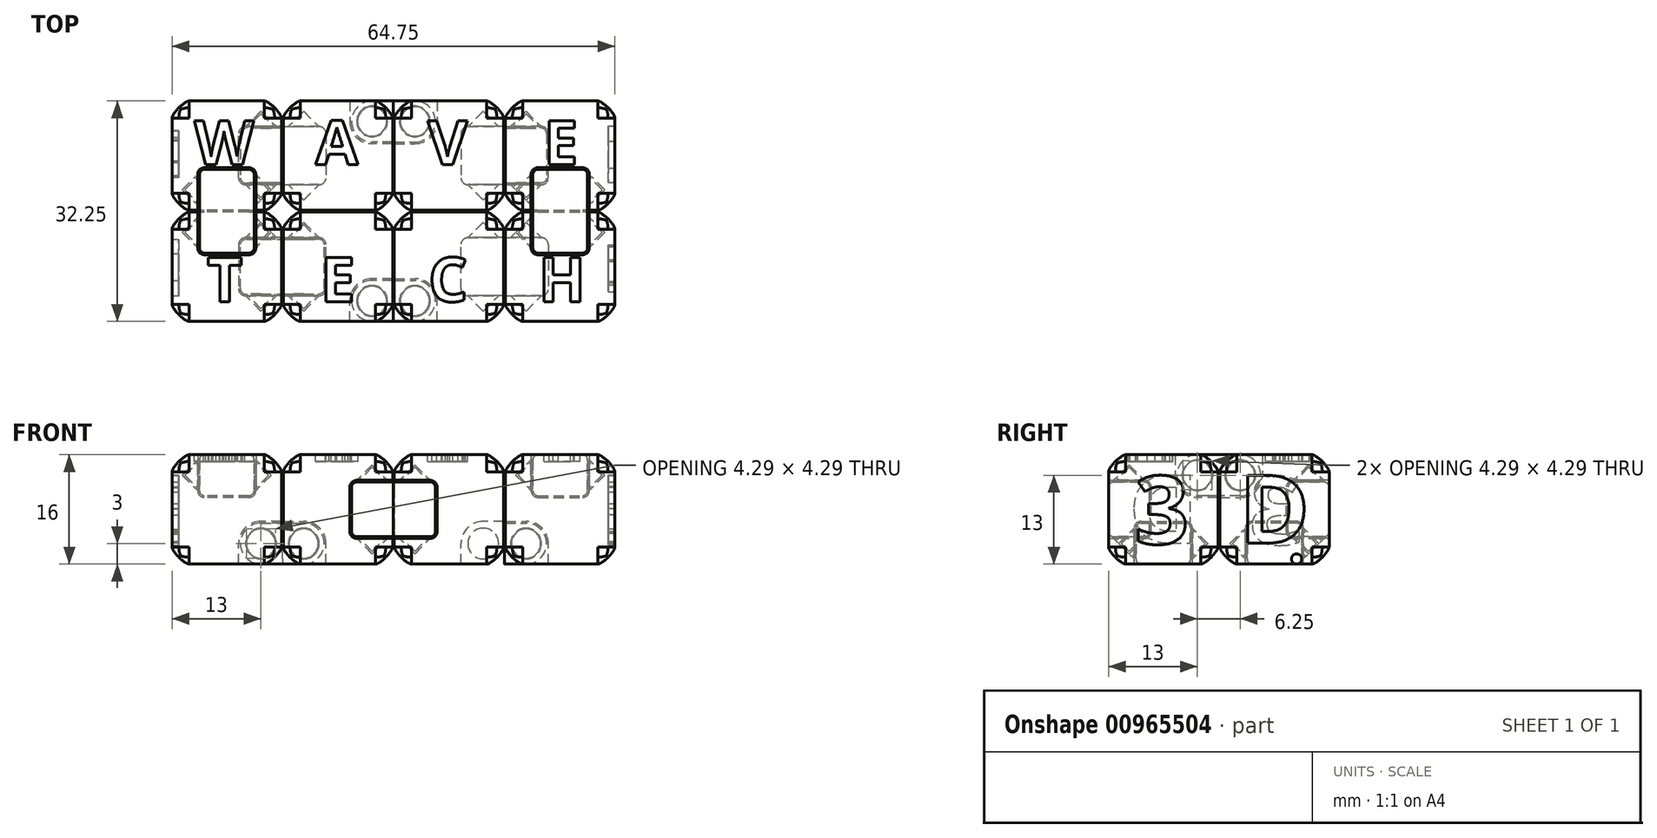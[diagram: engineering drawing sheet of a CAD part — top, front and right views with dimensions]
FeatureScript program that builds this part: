
annotation { "Feature Type Name" : "Feature", "Feature Type Description" : "" }
export const myFeature = defineFeature(function(context is Context, id is Id, definition is map)
    precondition{}
    {
        {
            assignVariable(context, id + "F0", {"name" : "cubeSize", "anyValue" : 16});
        }
        {
            assignVariable(context, id + "F1", {"name" : "hingeSize", "anyValue" : getVariable(context, 'cubeSize') / 2});
        }
        {
            assignVariable(context, id + "F2", {"name" : "hingeDiameter", "anyValue" : getVariable(context, 'hingeSize') / 2});
        }
        {
            assignVariable(context, id + "F3", {"name" : "minThickness", "anyValue" : 1});
        }
        {
            assignVariable(context, id + "F4", {"name" : "hingeGap", "anyValue" : .25});
        }
        {
            var Q0;
            Q0=qCreatedBy(makeId("Top.planeOp"),FACE);
            var sketch = newSketch(context, id + "F5", { "sketchPlane" : qUnion([Q0])});
            skLineSegment(sketch, "E0.bottom", {"start": v(8, -8) * mm, "end": v(-8, -8) * mm});
            skLineSegment(sketch, "E0.top", {"start": v(8, 8) * mm, "end": v(-8, 8) * mm});
            skLineSegment(sketch, "E0.left", {"start": v(8, -8) * mm, "end": v(8, 8) * mm});
            skLineSegment(sketch, "E0.right", {"start": v(-8, -8) * mm, "end": v(-8, 8) * mm});
            skPoint(sketch, "E0.middle", {"position": v(0, 0) * mm});
            skSolve(sketch);
        }
        {
            var Q0;
            Q0=qSketchRegion(id+"F5",true);
            extrude(context, id + "F6", {"entities" : qUnion([Q0]), "depth" : (getVariable(context, 'cubeSize')) * mm, "offsetDistance" : 25 * mm});
        }
        {
            var Q0;
            Q0=qCreatedBy(makeId("Front.planeOp"),FACE);
            var sketch = newSketch(context, id + "F7", { "sketchPlane" : qUnion([Q0])});
            skCircle(sketch, "E1", {"center": v(5, 3) * mm, "radius": 2 * mm});
            skLineSegment(sketch, "E2", {"start": v(5, 3) * mm, "end": v(7, 3) * mm, "construction": true});
            skLineSegment(sketch, "E3", {"start": v(7, 3) * mm, "end": v(8, 3) * mm, "construction": true});
            skLineSegment(sketch, "E4", {"start": v(5, 0) * mm, "end": v(5, 1) * mm, "construction": true});
            skLineSegment(sketch, "E5", {"start": v(5, 1) * mm, "end": v(5, 3) * mm, "construction": true});
            skLineSegment(sketch, "E6", {"start": v(8, 0) * mm, "end": v(1.75, 0) * mm});
            skLineSegment(sketch, "E7", {"start": v(1.75, 0) * mm, "end": v(1.75, 3) * mm});
            skLineSegment(sketch, "E8", {"start": v(8, 0) * mm, "end": v(8, 6.25) * mm});
            skLineSegment(sketch, "E9", {"start": v(8, 6.25) * mm, "end": v(5, 6.25) * mm});
            skArc(sketch, "E10", {"start": v(5, 6.25) * mm, "mid": v(2.7, 5.3) * mm, "end": v(1.75, 3) * mm});
            skSolve(sketch);
        }
        {
            var Q0;
            Q0=makeQuery(id+"F7.imprint","IMPRINT",FACE,{"disambiguationData":[TD([[makeQuery(id+"F7.imprint","IMPRINT",EDGE,{"derivedFrom":sQuery(id+"F7.wireOp",EDGE,"E1")}),-1.0]])]});
            var Q1;
            Q1=makeQuery(id+"F7.imprint","IMPRINT",FACE,{"disambiguationData":[TD([[makeQuery(id+"F7.imprint","IMPRINT",EDGE,{"derivedFrom":sQuery(id+"F7.wireOp",EDGE,"E1")}),1.0]])]});
            extrude(context, id + "F8", {"entities" : qUnion([Q0, Q1]), "operationType" : NewBodyOperationType.REMOVE, "endBound" : BoundingType.SYMMETRIC, "oppositeDirection" : true, "depth" : (getVariable(context, 'hingeSize') + getVariable(context, 'hingeGap') * 2) * mm, "offsetDistance" : 25 * mm});
        }
        {
            var Q0;
            Q0=makeQuery(id+"F6.opExtrude","CAP_VERTEX",VERTEX,{"disambiguationData":[OSD([sQuery(id+"F5.wireOp",EDGE,"E0.bottom"),sQuery(id+"F5.wireOp",EDGE,"E0.right")])],"isStart":false});
            var Q1;
            Q1=makeQuery(id+"F6.opExtrude","CAP_VERTEX",VERTEX,{"disambiguationData":[OSD([sQuery(id+"F5.wireOp",EDGE,"E0.bottom"),sQuery(id+"F5.wireOp",EDGE,"E0.left")])],"isStart":true});
            var Q2;
            Q2=makeQuery(id+"F6.opExtrude","CAP_VERTEX",VERTEX,{"disambiguationData":[OSD([sQuery(id+"F5.wireOp",EDGE,"E0.top"),sQuery(id+"F5.wireOp",EDGE,"E0.left")])],"isStart":true});
            cPlane(context, id + "F9", {"entities" : qUnion([Q0, Q1, Q2]), "cplaneType" : CPlaneType.THREE_POINT, "offset" : 25 * mm, "width" : 150 * mm, "height" : 150 * mm});
        }
        {
            var Q0;
            Q0=qCreatedBy(id+"F9.planeOp",FACE);
            var sketch = newSketch(context, id + "F10", { "sketchPlane" : qUnion([Q0])});
            skLineSegment(sketch, "E11", {"start": v(4.25, 0.84) * mm, "end": v(-4.25, 0.84) * mm});
            skLineSegment(sketch, "E12", {"start": v(-4.25, 0.84) * mm, "end": v(-6.5, -1.41) * mm});
            skLineSegment(sketch, "E13", {"start": v(-6.5, -1.41) * mm, "end": v(6.5, -1.41) * mm});
            skLineSegment(sketch, "E14", {"start": v(6.5, -1.41) * mm, "end": v(4.25, 0.84) * mm});
            skSolve(sketch);
        }
        {
            var Q0;
            Q0=makeQuery(id+"F10.imprint","IMPRINT",FACE,{"disambiguationData":[TD([[makeQuery(id+"F10.imprint","IMPRINT",EDGE,{"derivedFrom":sQuery(id+"F10.wireOp",EDGE,"E11")}),1.0]])]});
            var Q1;
            Q1=sQuery(id+"F10.wireOp",EDGE,"E13");
            revolve(context, id + "F11", {"operationType" : NewBodyOperationType.REMOVE, "entities" : qUnion([Q0]), "axis" : qUnion([Q1]), "revolveType" : RevolveType.FULL, "oppositeDirection" : true});
        }
        {
            var Q0;
            Q0=qCreatedBy(makeId("Right.planeOp"),FACE);
            var sketch = newSketch(context, id + "F12", { "sketchPlane" : qUnion([Q0])});
            skCircle(sketch, "E15", {"center": v(5, 13) * mm, "radius": 2 * mm});
            skLineSegment(sketch, "E16", {"start": v(1.75, 16) * mm, "end": v(8, 16) * mm});
            skLineSegment(sketch, "E17", {"start": v(8, 16) * mm, "end": v(8, 9.75) * mm});
            skLineSegment(sketch, "E18", {"start": v(8, 9.75) * mm, "end": v(5, 9.75) * mm});
            skLineSegment(sketch, "E19", {"start": v(1.75, 16) * mm, "end": v(1.75, 13) * mm});
            skLineSegment(sketch, "E20", {"start": v(5, 13) * mm, "end": v(7, 13) * mm, "construction": true});
            skLineSegment(sketch, "E21", {"start": v(7, 13) * mm, "end": v(8, 13) * mm, "construction": true});
            skLineSegment(sketch, "E22", {"start": v(5, 13) * mm, "end": v(5, 15) * mm, "construction": true});
            skLineSegment(sketch, "E23", {"start": v(5, 15) * mm, "end": v(5, 16) * mm, "construction": true});
            skArc(sketch, "E24", {"start": v(1.75, 13) * mm, "mid": v(2.7, 10.7) * mm, "end": v(5, 9.75) * mm});
            skSolve(sketch);
        }
        {
            var Q0;
            Q0=makeQuery(id+"F12.imprint","IMPRINT",FACE,{"disambiguationData":[TD([[makeQuery(id+"F12.imprint","IMPRINT",EDGE,{"derivedFrom":sQuery(id+"F12.wireOp",EDGE,"E15")}),1.0]])]});
            var Q1;
            Q1=makeQuery(id+"F12.imprint","IMPRINT",FACE,{"disambiguationData":[TD([[makeQuery(id+"F12.imprint","IMPRINT",EDGE,{"derivedFrom":sQuery(id+"F12.wireOp",EDGE,"E15")}),-1.0]])]});
            extrude(context, id + "F13", {"entities" : qUnion([Q0, Q1]), "operationType" : NewBodyOperationType.REMOVE, "endBound" : BoundingType.SYMMETRIC, "depth" : (getVariable(context, 'hingeSize') + getVariable(context, 'hingeGap') * 2) * mm, "offsetDistance" : 25 * mm});
        }
        {
            var Q0;
            Q0=makeQuery(id+"F6.opExtrude","CAP_VERTEX",VERTEX,{"disambiguationData":[OSD([sQuery(id+"F5.wireOp",EDGE,"E0.top"),sQuery(id+"F5.wireOp",EDGE,"E0.left")])],"isStart":false});
            var Q1;
            Q1=makeQuery(id+"F6.opExtrude","CAP_VERTEX",VERTEX,{"disambiguationData":[OSD([sQuery(id+"F5.wireOp",EDGE,"E0.top"),sQuery(id+"F5.wireOp",EDGE,"E0.right")])],"isStart":false});
            var Q2;
            Q2=makeQuery(id+"F6.opExtrude","CAP_VERTEX",VERTEX,{"disambiguationData":[OSD([sQuery(id+"F5.wireOp",EDGE,"E0.bottom"),sQuery(id+"F5.wireOp",EDGE,"E0.right")])],"isStart":true});
            cPlane(context, id + "F14", {"entities" : qUnion([Q0, Q1, Q2]), "cplaneType" : CPlaneType.THREE_POINT, "offset" : 25 * mm, "width" : 150 * mm, "height" : 150 * mm});
        }
        {
            var Q0;
            Q0=qCreatedBy(id+"F14.planeOp",FACE);
            var sketch = newSketch(context, id + "F15", { "sketchPlane" : qUnion([Q0])});
            skLineSegment(sketch, "E25", {"start": v(-6.5, 12.73) * mm, "end": v(6.5, 12.73) * mm});
            skLineSegment(sketch, "E26", {"start": v(6.5, 12.73) * mm, "end": v(4.25, 10.48) * mm});
            skLineSegment(sketch, "E27", {"start": v(4.25, 10.48) * mm, "end": v(-4.25, 10.48) * mm});
            skLineSegment(sketch, "E28", {"start": v(-4.25, 10.48) * mm, "end": v(-6.5, 12.73) * mm});
            skSolve(sketch);
        }
        {
            var Q0;
            Q0=qSketchRegion(id+"F15",true);
            var Q1;
            Q1=sQuery(id+"F15.wireOp",EDGE,"E25");
            revolve(context, id + "F16", {"operationType" : NewBodyOperationType.REMOVE, "entities" : qUnion([Q0]), "axis" : qUnion([Q1]), "revolveType" : RevolveType.FULL, "oppositeDirection" : true});
        }
        {
            var Q0;
            Q0=makeQuery(id+"F6.opExtrude","SWEPT_FACE",FACE,{"disambiguationData":[OSD([sQuery(id+"F5.wireOp",EDGE,"E0.right")])]});
            var Q1;
            Q1=makeQuery(id+"F6.opExtrude","SWEPT_FACE",FACE,{"disambiguationData":[OSD([sQuery(id+"F5.wireOp",EDGE,"E0.bottom")])]});
            var Q2;
            {var subQ0=sQuery(id+"F5.wireOp",EDGE,"E0.right");var subQ1=sQuery(id+"F5.wireOp",EDGE,"E0.top");Q2=makeQuery(id+"F13.boolean.opBoolean","SPLIT",EDGE,{"disambiguationData":[TD([makeQuery(id+"F6.opExtrude","SWEPT_FACE",FACE,{"disambiguationData":[OSD([subQ0])]})])],"derivedFrom":makeQuery(id+"F6.opExtrude","CAP_EDGE",EDGE,{"disambiguationData":[OSD([subQ1])],"isStart":false})});}
            var Q3;
            {var subQ0=sQuery(id+"F5.wireOp",EDGE,"E0.left");var subQ1=sQuery(id+"F5.wireOp",EDGE,"E0.top");Q3=makeQuery(id+"F13.boolean.opBoolean","SPLIT",EDGE,{"disambiguationData":[TD([makeQuery(id+"F6.opExtrude","SWEPT_FACE",FACE,{"disambiguationData":[OSD([subQ0])]})])],"derivedFrom":makeQuery(id+"F6.opExtrude","CAP_EDGE",EDGE,{"disambiguationData":[OSD([subQ1])],"isStart":false})});}
            var Q4;
            Q4=makeQuery(id+"F6.opExtrude","CAP_EDGE",EDGE,{"disambiguationData":[OSD([sQuery(id+"F5.wireOp",EDGE,"E0.left")])],"isStart":false});
            var Q5;
            Q5=makeQuery(id+"F6.opExtrude","SWEPT_EDGE",EDGE,{"disambiguationData":[OSD([sQuery(id+"F5.wireOp",EDGE,"E0.top"),sQuery(id+"F5.wireOp",EDGE,"E0.left")])]});
            var Q6;
            {var subQ0=sQuery(id+"F5.wireOp",EDGE,"E0.left");var subQ1=sQuery(id+"F5.wireOp",EDGE,"E0.top");Q6=makeQuery(id+"F8.boolean.opBoolean","SPLIT",EDGE,{"disambiguationData":[TD([makeQuery(id+"F6.opExtrude","SWEPT_FACE",FACE,{"disambiguationData":[OSD([subQ1])]})])],"derivedFrom":makeQuery(id+"F6.opExtrude","CAP_EDGE",EDGE,{"disambiguationData":[OSD([subQ0])],"isStart":true})});}
            var Q7;
            Q7=makeQuery(id+"F6.opExtrude","CAP_EDGE",EDGE,{"disambiguationData":[OSD([sQuery(id+"F5.wireOp",EDGE,"E0.top")])],"isStart":true});
            var Q8;
            {var subQ0=sQuery(id+"F5.wireOp",EDGE,"E0.bottom");var subQ1=sQuery(id+"F5.wireOp",EDGE,"E0.left");Q8=makeQuery(id+"F8.boolean.opBoolean","SPLIT",EDGE,{"disambiguationData":[TD([makeQuery(id+"F6.opExtrude","SWEPT_FACE",FACE,{"disambiguationData":[OSD([subQ0])]})])],"derivedFrom":makeQuery(id+"F6.opExtrude","CAP_EDGE",EDGE,{"disambiguationData":[OSD([subQ1])],"isStart":true})});}
            fillet(context, id + "F17", {"entities" : qUnion([Q0, Q1, Q2, Q3, Q4, Q5, Q6, Q7, Q8]), "radius" : (getVariable(context, 'hingeDiameter') / 2 + getVariable(context, 'minThickness') - .5) * mm, "tangentPropagation" : true, "rho" : .2, "crossSection" : FilletCrossSection.CONIC, "allowEdgeOverflow" : false});
        }
        {
            var Q0;
            Q0=makeQuery(id+"F8.boolean.opBoolean","COPY",EDGE,{"derivedFrom":makeQuery(id+"F8.opExtrude","CAP_EDGE",EDGE,{"disambiguationData":[OSD([sQuery(id+"F7.wireOp",EDGE,"E7")])],"isStart":true})});
            var Q1;
            Q1=makeQuery(id+"F8.boolean.opBoolean","COPY",EDGE,{"derivedFrom":makeQuery(id+"F8.opExtrude","CAP_EDGE",EDGE,{"disambiguationData":[OSD([sQuery(id+"F7.wireOp",EDGE,"E7")])],"isStart":false})});
            var Q2;
            Q2=makeQuery(id+"F13.boolean.opBoolean","COPY",EDGE,{"derivedFrom":makeQuery(id+"F13.opExtrude","CAP_EDGE",EDGE,{"disambiguationData":[OSD([sQuery(id+"F12.wireOp",EDGE,"E18")])],"isStart":false})});
            var Q3;
            Q3=makeQuery(id+"F13.boolean.opBoolean","COPY",EDGE,{"derivedFrom":makeQuery(id+"F13.opExtrude","CAP_EDGE",EDGE,{"disambiguationData":[OSD([sQuery(id+"F12.wireOp",EDGE,"E18")])],"isStart":true})});
            fillet(context, id + "F18", {"entities" : qUnion([Q0, Q1, Q2, Q3]), "radius" : (getVariable(context, 'minThickness')) * mm, "tangentPropagation" : true, "allowEdgeOverflow" : false});
        }
        {
            var Q0;
            Q0=qCreatedBy(makeId("Front.planeOp"),FACE);
            var sketch = newSketch(context, id + "F19", { "sketchPlane" : qUnion([Q0])});
            skCircle(sketch, "E29", {"center": v(5, 3) * mm, "radius": 2 * mm, "construction": true});
            skArc(sketch, "E30", {"start": v(5, 6) * mm, "mid": v(2, 3) * mm, "end": v(5, 0) * mm});
            skArc(sketch, "E31", {"start": v(11.25, 0) * mm, "mid": v(14.25, 3) * mm, "end": v(11.25, 6) * mm});
            skLineSegment(sketch, "E32", {"start": v(5, 3) * mm, "end": v(8, 3) * mm, "construction": true});
            skCircle(sketch, "E33", {"center": v(11.25, 3) * mm, "radius": 2 * mm, "construction": true});
            skLineSegment(sketch, "E34", {"start": v(8, 3) * mm, "end": v(8.25, 3) * mm, "construction": true});
            skLineSegment(sketch, "E35", {"start": v(8.25, 3) * mm, "end": v(11.25, 3) * mm, "construction": true});
            skLineSegment(sketch, "E36", {"start": v(8.12, 0) * mm, "end": v(8.12, 3) * mm});
            skLineSegment(sketch, "E37", {"start": v(8.12, 3) * mm, "end": v(8.12, 6) * mm});
            skLineSegment(sketch, "E38", {"start": v(11.25, 0) * mm, "end": v(5, 0) * mm});
            skLineSegment(sketch, "E39", {"start": v(11.25, 6) * mm, "end": v(5, 6) * mm});
            skSolve(sketch);
        }
        {
            var Q0;
            Q0=makeQuery(id+"F19.imprint","IMPRINT",FACE,{"disambiguationData":[TD([[makeQuery(id+"F19.imprint","IMPRINT",EDGE,{"derivedFrom":sQuery(id+"F19.wireOp",EDGE,"E30")}),1.0]])]});
            extrude(context, id + "F20", {"entities" : qUnion([Q0]), "endBound" : BoundingType.SYMMETRIC, "depth" : (getVariable(context, 'hingeSize')) * mm, "offsetDistance" : 25 * mm});
        }
        {
            var Q0;
            Q0=qCreatedBy(id+"F9.planeOp",FACE);
            var sketch = newSketch(context, id + "F21", { "sketchPlane" : qUnion([Q0])});
            skLineSegment(sketch, "E40", {"start": v(6.15, -1.41) * mm, "end": v(3.9, 0.84) * mm});
            skLineSegment(sketch, "E41", {"start": v(3.9, 0.84) * mm, "end": v(-3.9, 0.84) * mm});
            skLineSegment(sketch, "E42", {"start": v(-3.9, 0.84) * mm, "end": v(-6.15, -1.41) * mm});
            skLineSegment(sketch, "E43", {"start": v(-6.15, -1.41) * mm, "end": v(6.15, -1.41) * mm});
            skSolve(sketch);
        }
        {
            var Q0;
            Q0=qSketchRegion(id+"F21",true);
            var Q1;
            Q1=sQuery(id+"F21.wireOp",EDGE,"E43");
            revolve(context, id + "F22", {"operationType" : NewBodyOperationType.ADD, "entities" : qUnion([Q0]), "axis" : qUnion([Q1]), "revolveType" : RevolveType.FULL});
        }
        {
            var Q0;
            Q0=qCreatedBy(makeId("Right.planeOp"),FACE);
            var sketch = newSketch(context, id + "F23", { "sketchPlane" : qUnion([Q0])});
            skCircle(sketch, "E44", {"center": v(5, 13) * mm, "radius": 2.25 * mm, "construction": true});
            skArc(sketch, "E45", {"start": v(5, 16) * mm, "mid": v(2, 13) * mm, "end": v(5, 10) * mm});
            skArc(sketch, "E46", {"start": v(11.25, 10) * mm, "mid": v(14.25, 13) * mm, "end": v(11.25, 16) * mm});
            skLineSegment(sketch, "E47", {"start": v(5, 13) * mm, "end": v(8, 13) * mm, "construction": true});
            skCircle(sketch, "E48", {"center": v(11.25, 13) * mm, "radius": 2 * mm, "construction": true});
            skLineSegment(sketch, "E49", {"start": v(8, 13) * mm, "end": v(8.25, 13) * mm, "construction": true});
            skLineSegment(sketch, "E50", {"start": v(8.25, 13) * mm, "end": v(11.25, 13) * mm, "construction": true});
            skLineSegment(sketch, "E51", {"start": v(8.12, 10) * mm, "end": v(8.12, 13) * mm});
            skLineSegment(sketch, "E52", {"start": v(8.12, 13) * mm, "end": v(8.12, 16) * mm});
            skLineSegment(sketch, "E53", {"start": v(11.25, 10) * mm, "end": v(5, 10) * mm});
            skLineSegment(sketch, "E54", {"start": v(11.25, 16) * mm, "end": v(5, 16) * mm});
            skSolve(sketch);
        }
        {
            var Q0;
            {var subQ3=sQuery(id+"F23.wireOp",EDGE,"E45");Q0=makeQuery(id+"F23.imprint","IMPRINT",FACE,{"disambiguationData":[TD([[makeQuery(id+"F23.imprint","IMPRINT",EDGE,{"derivedFrom":subQ3}),1.0]])]});}
            extrude(context, id + "F24", {"entities" : qUnion([Q0]), "endBound" : BoundingType.SYMMETRIC, "depth" : (getVariable(context, 'hingeSize')) * mm, "offsetDistance" : 25 * mm});
        }
        {
            var Q0;
            Q0=makeQuery(id+"F20.opExtrude","CAP_EDGE",EDGE,{"disambiguationData":[OSD([sQuery(id+"F19.wireOp",EDGE,"E38")])],"isStart":false});
            var Q1;
            Q1=makeQuery(id+"F20.opExtrude","CAP_EDGE",EDGE,{"disambiguationData":[OSD([sQuery(id+"F19.wireOp",EDGE,"E38")])],"isStart":true});
            var Q2;
            Q2=makeQuery(id+"F24.opExtrude","CAP_EDGE",EDGE,{"disambiguationData":[OSD([sQuery(id+"F23.wireOp",EDGE,"E54")])],"isStart":false});
            var Q3;
            Q3=makeQuery(id+"F24.opExtrude","CAP_EDGE",EDGE,{"disambiguationData":[OSD([sQuery(id+"F23.wireOp",EDGE,"E54")])],"isStart":true});
            fillet(context, id + "F25", {"entities" : qUnion([Q0, Q1, Q2, Q3]), "radius" : (getVariable(context, 'minThickness') - getVariable(context, 'hingeGap')) * mm, "tangentPropagation" : true, "allowEdgeOverflow" : false});
        }
        {
            var Q0;
            Q0=qCreatedBy(id+"F14.planeOp",FACE);
            var sketch = newSketch(context, id + "F26", { "sketchPlane" : qUnion([Q0])});
            skLineSegment(sketch, "E55", {"start": v(-6.15, 12.73) * mm, "end": v(6.15, 12.73) * mm});
            skLineSegment(sketch, "E56", {"start": v(6.15, 12.73) * mm, "end": v(3.9, 10.48) * mm});
            skLineSegment(sketch, "E57", {"start": v(3.9, 10.48) * mm, "end": v(-3.9, 10.48) * mm});
            skLineSegment(sketch, "E58", {"start": v(-3.9, 10.48) * mm, "end": v(-6.15, 12.73) * mm});
            skSolve(sketch);
        }
        {
            var Q0;
            Q0=makeQuery(id+"F26.imprint","IMPRINT",FACE,{"disambiguationData":[TD([[makeQuery(id+"F26.imprint","IMPRINT",EDGE,{"derivedFrom":sQuery(id+"F26.wireOp",EDGE,"E55")}),-1.0]])]});
            var Q1;
            Q1=sQuery(id+"F26.wireOp",EDGE,"E55");
            revolve(context, id + "F27", {"operationType" : NewBodyOperationType.ADD, "entities" : qUnion([Q0]), "axis" : qUnion([Q1]), "revolveType" : RevolveType.FULL});
        }
        {
            var Q0;
            Q0=makeQuery(id+"F20.opExtrude","SWEPT_FACE",FACE,{"disambiguationData":[OSD([sQuery(id+"F19.wireOp",EDGE,"E36"),sQuery(id+"F19.wireOp",EDGE,"E37")])]});
            var sketch = newSketch(context, id + "F28", { "sketchPlane" : qUnion([Q0])});
            skLineSegment(sketch, "E59", {"start": v(-7.63, -0.12) * mm, "end": v(6.67, -0.12) * mm, "construction": true});
            skSolve(sketch);
        }
        {
            var Q0;
            Q0=makeQuery(id+"F6.opExtrude","SWEPT_BODY",BODY,{"disambiguationData":[OSD([sQuery(id+"F5.wireOp",EDGE,"E0.bottom"),sQuery(id+"F5.wireOp",EDGE,"E0.top"),sQuery(id+"F5.wireOp",EDGE,"E0.left"),sQuery(id+"F5.wireOp",EDGE,"E0.right")])]});
            var Q1;
            Q1=makeQuery(id+"F24.opExtrude","SWEPT_BODY",BODY,{"disambiguationData":[OSD([sQuery(id+"F23.wireOp",EDGE,"E45"),sQuery(id+"F23.wireOp",EDGE,"E51"),sQuery(id+"F23.wireOp",EDGE,"E52"),sQuery(id+"F23.wireOp",EDGE,"E53"),sQuery(id+"F23.wireOp",EDGE,"E54")])]});
            var Q2;
            Q2=sQuery(id+"F28.wireOp",EDGE,"E59");
            circularPattern(context, id + "F29", {"entities" : qUnion([Q0, Q1]), "axis" : qUnion([Q2]), "angle" : 90 * degree, "instanceCount" : 2});
        }
        {
            var Q0;
            Q0=makeQuery(id+"F29.opPattern","COPY",BODY,{"derivedFrom":makeQuery(id+"F6.opExtrude","SWEPT_BODY",BODY,{"disambiguationData":[OSD([sQuery(id+"F5.wireOp",EDGE,"E0.bottom"),sQuery(id+"F5.wireOp",EDGE,"E0.top"),sQuery(id+"F5.wireOp",EDGE,"E0.left"),sQuery(id+"F5.wireOp",EDGE,"E0.right")])]}),"instanceName":"1"});
            var Q1;
            Q1=makeQuery(id+"F29.opPattern","COPY",BODY,{"derivedFrom":makeQuery(id+"F24.opExtrude","SWEPT_BODY",BODY,{"disambiguationData":[OSD([sQuery(id+"F23.wireOp",EDGE,"E45"),sQuery(id+"F23.wireOp",EDGE,"E51"),sQuery(id+"F23.wireOp",EDGE,"E52"),sQuery(id+"F23.wireOp",EDGE,"E53"),sQuery(id+"F23.wireOp",EDGE,"E54")])]}),"instanceName":"1"});
            var Q2;
            Q2=qCreatedBy(makeId("Front.planeOp"),FACE);
            mirror(context, id + "F30", {"entities" : qUnion([Q0, Q1]), "mirrorPlane" : qUnion([Q2])});
        }
        {
            var Q0;
            Q0=makeQuery(id+"F29.opPattern","COPY",BODY,{"derivedFrom":makeQuery(id+"F24.opExtrude","SWEPT_BODY",BODY,{"disambiguationData":[OSD([sQuery(id+"F23.wireOp",EDGE,"E45"),sQuery(id+"F23.wireOp",EDGE,"E51"),sQuery(id+"F23.wireOp",EDGE,"E52"),sQuery(id+"F23.wireOp",EDGE,"E53"),sQuery(id+"F23.wireOp",EDGE,"E54")])]}),"instanceName":"1"});
            var Q1;
            Q1=makeQuery(id+"F29.opPattern","COPY",BODY,{"derivedFrom":makeQuery(id+"F6.opExtrude","SWEPT_BODY",BODY,{"disambiguationData":[OSD([sQuery(id+"F5.wireOp",EDGE,"E0.bottom"),sQuery(id+"F5.wireOp",EDGE,"E0.top"),sQuery(id+"F5.wireOp",EDGE,"E0.left"),sQuery(id+"F5.wireOp",EDGE,"E0.right")])]}),"instanceName":"1"});
            deleteBodies(context, id + "F31", {"entities" : qUnion([Q0, Q1])});
        }
        {
            var Q0;
            Q0=makeQuery(id+"F20.opExtrude","SWEPT_BODY",BODY,{"disambiguationData":[OSD([sQuery(id+"F19.wireOp",EDGE,"E30"),sQuery(id+"F19.wireOp",EDGE,"E36"),sQuery(id+"F19.wireOp",EDGE,"E37"),sQuery(id+"F19.wireOp",EDGE,"E38"),sQuery(id+"F19.wireOp",EDGE,"E39")])]});
            var Q1;
            Q1=makeQuery(id+"F20.opExtrude","SWEPT_FACE",FACE,{"disambiguationData":[OSD([sQuery(id+"F19.wireOp",EDGE,"E36"),sQuery(id+"F19.wireOp",EDGE,"E37")])]});
            mirror(context, id + "F32", {"operationType" : NewBodyOperationType.ADD, "entities" : qUnion([Q0]), "mirrorPlane" : qUnion([Q1])});
        }
        {
            var Q0;
            {var subQ0=sQuery(id+"F5.wireOp",EDGE,"E0.left");var subQ1=makeQuery(id+"F6.opExtrude","SWEPT_FACE",FACE,{"disambiguationData":[OSD([subQ0])]});var subQ2=sQuery(id+"F5.wireOp",EDGE,"E0.bottom");Q0=makeQuery(id+"F30.opPattern","COPY",VERTEX,{"derivedFrom":makeQuery(id+"F29.opPattern","COPY",VERTEX,{"derivedFrom":makeQuery(id+"F17.opFillet","BLEND_VERTEX",VERTEX,{"blendedFrom":[makeQuery(id+"F6.opExtrude","CAP_VERTEX",VERTEX,{"disambiguationData":[OSD([subQ2,subQ0])],"isStart":true}),makeQuery(id+"F6.opExtrude","SWEPT_EDGE",EDGE,{"disambiguationData":[OSD([subQ2,subQ0])]}),makeQuery(id+"F8.boolean.opBoolean","SPLIT",EDGE,{"disambiguationData":[TD([makeQuery(id+"F6.opExtrude","SWEPT_FACE",FACE,{"disambiguationData":[OSD([subQ2])]})])],"derivedFrom":makeQuery(id+"F6.opExtrude","CAP_EDGE",EDGE,{"disambiguationData":[OSD([subQ0])],"isStart":true})}),subQ1],"blendedInto":[subQ1]}),"instanceName":"1"}),"instanceName":"1"});}
            var Q1;
            {var subQ0=sQuery(id+"F5.wireOp",EDGE,"E0.left");var subQ1=sQuery(id+"F5.wireOp",EDGE,"E0.top");Q1=makeQuery(id+"F30.opPattern","COPY",VERTEX,{"derivedFrom":makeQuery(id+"F29.opPattern","COPY",VERTEX,{"derivedFrom":makeQuery(id+"F17.opFillet","BLEND_VERTEX",VERTEX,{"blendedFrom":[makeQuery(id+"F6.opExtrude","CAP_VERTEX",VERTEX,{"disambiguationData":[OSD([subQ1,subQ0])],"isStart":false}),makeQuery(id+"F6.opExtrude","SWEPT_EDGE",EDGE,{"disambiguationData":[OSD([subQ1,subQ0])]}),makeQuery(id+"F6.opExtrude","CAP_EDGE",EDGE,{"disambiguationData":[OSD([subQ0])],"isStart":false}),makeQuery(id+"F6.opExtrude","SWEPT_FACE",FACE,{"disambiguationData":[OSD([subQ0])]})],"blendedInto":[makeQuery(id+"F6.opExtrude","SWEPT_FACE",FACE,{"disambiguationData":[OSD([subQ0])]})]}),"instanceName":"1"}),"instanceName":"1"});}
            var Q2;
            {var subQ0=sQuery(id+"F5.wireOp",EDGE,"E0.right");var subQ1=sQuery(id+"F5.wireOp",EDGE,"E0.top");Q2=makeQuery(id+"F30.opPattern","COPY",VERTEX,{"derivedFrom":makeQuery(id+"F29.opPattern","COPY",VERTEX,{"derivedFrom":makeQuery(id+"F17.opFillet","BLEND_VERTEX",VERTEX,{"blendedFrom":[makeQuery(id+"F6.opExtrude","CAP_VERTEX",VERTEX,{"disambiguationData":[OSD([subQ1,subQ0])],"isStart":false}),makeQuery(id+"F6.opExtrude","SWEPT_EDGE",EDGE,{"disambiguationData":[OSD([subQ1,subQ0])]}),makeQuery(id+"F6.opExtrude","CAP_EDGE",EDGE,{"disambiguationData":[OSD([subQ0])],"isStart":false}),makeQuery(id+"F6.opExtrude","SWEPT_FACE",FACE,{"disambiguationData":[OSD([subQ0])]})],"blendedInto":[makeQuery(id+"F6.opExtrude","SWEPT_FACE",FACE,{"disambiguationData":[OSD([subQ0])]})]}),"instanceName":"1"}),"instanceName":"1"});}
            cPlane(context, id + "F33", {"entities" : qUnion([Q0, Q1, Q2]), "cplaneType" : CPlaneType.THREE_POINT, "offset" : 25 * mm, "width" : 150 * mm, "height" : 150 * mm});
        }
        {
            var Q0;
            Q0=qCreatedBy(id+"F33.planeOp",FACE);
            var sketch = newSketch(context, id + "F34", { "sketchPlane" : qUnion([Q0])});
            skLineSegment(sketch, "E60", {"start": v(-18.56, 14.15) * mm, "end": v(-18.56, 1.85) * mm, "construction": true});
            skSolve(sketch);
        }
        {
            var Q0;
            Q0=makeQuery(id+"F30.opPattern","COPY",BODY,{"derivedFrom":makeQuery(id+"F29.opPattern","COPY",BODY,{"derivedFrom":makeQuery(id+"F24.opExtrude","SWEPT_BODY",BODY,{"disambiguationData":[OSD([sQuery(id+"F23.wireOp",EDGE,"E45"),sQuery(id+"F23.wireOp",EDGE,"E51"),sQuery(id+"F23.wireOp",EDGE,"E52"),sQuery(id+"F23.wireOp",EDGE,"E53"),sQuery(id+"F23.wireOp",EDGE,"E54")])]}),"instanceName":"1"}),"instanceName":"1"});
            var Q1;
            Q1=sQuery(id+"F34.wireOp",EDGE,"E60");
            circularPattern(context, id + "F35", {"entities" : qUnion([Q0]), "axis" : qUnion([Q1]), "angle" : 90 * degree, "instanceCount" : 2, "oppositeDirection" : true});
        }
        {
            var Q0;
            Q0=makeQuery(id+"F30.opPattern","COPY",BODY,{"derivedFrom":makeQuery(id+"F29.opPattern","COPY",BODY,{"derivedFrom":makeQuery(id+"F24.opExtrude","SWEPT_BODY",BODY,{"disambiguationData":[OSD([sQuery(id+"F23.wireOp",EDGE,"E45"),sQuery(id+"F23.wireOp",EDGE,"E51"),sQuery(id+"F23.wireOp",EDGE,"E52"),sQuery(id+"F23.wireOp",EDGE,"E53"),sQuery(id+"F23.wireOp",EDGE,"E54")])]}),"instanceName":"1"}),"instanceName":"1"});
            deleteBodies(context, id + "F36", {"entities" : qUnion([Q0])});
        }
        {
            var Q0;
            Q0=makeQuery(id+"F24.opExtrude","SWEPT_BODY",BODY,{"disambiguationData":[OSD([sQuery(id+"F23.wireOp",EDGE,"E45"),sQuery(id+"F23.wireOp",EDGE,"E51"),sQuery(id+"F23.wireOp",EDGE,"E52"),sQuery(id+"F23.wireOp",EDGE,"E53"),sQuery(id+"F23.wireOp",EDGE,"E54")])]});
            var Q1;
            Q1=makeQuery(id+"F6.opExtrude","SWEPT_BODY",BODY,{"disambiguationData":[OSD([sQuery(id+"F5.wireOp",EDGE,"E0.bottom"),sQuery(id+"F5.wireOp",EDGE,"E0.top"),sQuery(id+"F5.wireOp",EDGE,"E0.left"),sQuery(id+"F5.wireOp",EDGE,"E0.right")])]});
            var Q2;
            Q2=makeQuery(id+"F20.opExtrude","SWEPT_BODY",BODY,{"disambiguationData":[OSD([sQuery(id+"F19.wireOp",EDGE,"E30"),sQuery(id+"F19.wireOp",EDGE,"E36"),sQuery(id+"F19.wireOp",EDGE,"E37"),sQuery(id+"F19.wireOp",EDGE,"E38"),sQuery(id+"F19.wireOp",EDGE,"E39")])]});
            var Q3;
            Q3=makeQuery(id+"F30.opPattern","COPY",BODY,{"derivedFrom":makeQuery(id+"F29.opPattern","COPY",BODY,{"derivedFrom":makeQuery(id+"F6.opExtrude","SWEPT_BODY",BODY,{"disambiguationData":[OSD([sQuery(id+"F5.wireOp",EDGE,"E0.bottom"),sQuery(id+"F5.wireOp",EDGE,"E0.top"),sQuery(id+"F5.wireOp",EDGE,"E0.left"),sQuery(id+"F5.wireOp",EDGE,"E0.right")])]}),"instanceName":"1"}),"instanceName":"1"});
            var Q4;
            Q4=makeQuery(id+"F35.opPattern","COPY",BODY,{"derivedFrom":makeQuery(id+"F30.opPattern","COPY",BODY,{"derivedFrom":makeQuery(id+"F29.opPattern","COPY",BODY,{"derivedFrom":makeQuery(id+"F24.opExtrude","SWEPT_BODY",BODY,{"disambiguationData":[OSD([sQuery(id+"F23.wireOp",EDGE,"E45"),sQuery(id+"F23.wireOp",EDGE,"E51"),sQuery(id+"F23.wireOp",EDGE,"E52"),sQuery(id+"F23.wireOp",EDGE,"E53"),sQuery(id+"F23.wireOp",EDGE,"E54")])]}),"instanceName":"1"}),"instanceName":"1"}),"instanceName":"1"});
            var Q5;
            Q5=makeQuery(id+"F24.opExtrude","SWEPT_FACE",FACE,{"disambiguationData":[OSD([sQuery(id+"F23.wireOp",EDGE,"E51"),sQuery(id+"F23.wireOp",EDGE,"E52")])]});
            mirror(context, id + "F37", {"operationType" : NewBodyOperationType.ADD, "entities" : qUnion([Q0, Q1, Q2, Q3, Q4]), "mirrorPlane" : qUnion([Q5])});
        }
        {
            var Q0;
            Q0=makeQuery(id+"F35.opPattern","COPY",BODY,{"derivedFrom":makeQuery(id+"F30.opPattern","COPY",BODY,{"derivedFrom":makeQuery(id+"F29.opPattern","COPY",BODY,{"derivedFrom":makeQuery(id+"F24.opExtrude","SWEPT_BODY",BODY,{"disambiguationData":[OSD([sQuery(id+"F23.wireOp",EDGE,"E45"),sQuery(id+"F23.wireOp",EDGE,"E51"),sQuery(id+"F23.wireOp",EDGE,"E52"),sQuery(id+"F23.wireOp",EDGE,"E53"),sQuery(id+"F23.wireOp",EDGE,"E54")])]}),"instanceName":"1"}),"instanceName":"1"}),"instanceName":"1"});
            var Q1;
            Q1=makeQuery(id+"F37.opPattern","COPY",BODY,{"derivedFrom":makeQuery(id+"F35.opPattern","COPY",BODY,{"derivedFrom":makeQuery(id+"F30.opPattern","COPY",BODY,{"derivedFrom":makeQuery(id+"F29.opPattern","COPY",BODY,{"derivedFrom":makeQuery(id+"F24.opExtrude","SWEPT_BODY",BODY,{"disambiguationData":[OSD([sQuery(id+"F23.wireOp",EDGE,"E45"),sQuery(id+"F23.wireOp",EDGE,"E51"),sQuery(id+"F23.wireOp",EDGE,"E52"),sQuery(id+"F23.wireOp",EDGE,"E53"),sQuery(id+"F23.wireOp",EDGE,"E54")])]}),"instanceName":"1"}),"instanceName":"1"}),"instanceName":"1"}),"instanceName":"1"});
            var Q2;
            Q2=makeQuery(id+"F24.opExtrude","SWEPT_BODY",BODY,{"disambiguationData":[OSD([sQuery(id+"F23.wireOp",EDGE,"E45"),sQuery(id+"F23.wireOp",EDGE,"E51"),sQuery(id+"F23.wireOp",EDGE,"E52"),sQuery(id+"F23.wireOp",EDGE,"E53"),sQuery(id+"F23.wireOp",EDGE,"E54")])]});
            var Q3;
            Q3=makeQuery(id+"F37.opPattern","COPY",BODY,{"derivedFrom":makeQuery(id+"F20.opExtrude","SWEPT_BODY",BODY,{"disambiguationData":[OSD([sQuery(id+"F19.wireOp",EDGE,"E30"),sQuery(id+"F19.wireOp",EDGE,"E36"),sQuery(id+"F19.wireOp",EDGE,"E37"),sQuery(id+"F19.wireOp",EDGE,"E38"),sQuery(id+"F19.wireOp",EDGE,"E39")])]}),"instanceName":"1"});
            var Q4;
            Q4=makeQuery(id+"F20.opExtrude","SWEPT_BODY",BODY,{"disambiguationData":[OSD([sQuery(id+"F19.wireOp",EDGE,"E30"),sQuery(id+"F19.wireOp",EDGE,"E36"),sQuery(id+"F19.wireOp",EDGE,"E37"),sQuery(id+"F19.wireOp",EDGE,"E38"),sQuery(id+"F19.wireOp",EDGE,"E39")])]});
            var Q5;
            Q5=makeQuery(id+"F37.opPattern","COPY",BODY,{"derivedFrom":makeQuery(id+"F30.opPattern","COPY",BODY,{"derivedFrom":makeQuery(id+"F29.opPattern","COPY",BODY,{"derivedFrom":makeQuery(id+"F6.opExtrude","SWEPT_BODY",BODY,{"disambiguationData":[OSD([sQuery(id+"F5.wireOp",EDGE,"E0.bottom"),sQuery(id+"F5.wireOp",EDGE,"E0.top"),sQuery(id+"F5.wireOp",EDGE,"E0.left"),sQuery(id+"F5.wireOp",EDGE,"E0.right")])]}),"instanceName":"1"}),"instanceName":"1"}),"instanceName":"1"});
            var Q6;
            Q6=makeQuery(id+"F37.opPattern","COPY",BODY,{"derivedFrom":makeQuery(id+"F6.opExtrude","SWEPT_BODY",BODY,{"disambiguationData":[OSD([sQuery(id+"F5.wireOp",EDGE,"E0.bottom"),sQuery(id+"F5.wireOp",EDGE,"E0.top"),sQuery(id+"F5.wireOp",EDGE,"E0.left"),sQuery(id+"F5.wireOp",EDGE,"E0.right")])]}),"instanceName":"1"});
            var Q7;
            Q7=makeQuery(id+"F6.opExtrude","SWEPT_BODY",BODY,{"disambiguationData":[OSD([sQuery(id+"F5.wireOp",EDGE,"E0.bottom"),sQuery(id+"F5.wireOp",EDGE,"E0.top"),sQuery(id+"F5.wireOp",EDGE,"E0.left"),sQuery(id+"F5.wireOp",EDGE,"E0.right")])]});
            var Q8;
            Q8=makeQuery(id+"F30.opPattern","COPY",BODY,{"derivedFrom":makeQuery(id+"F29.opPattern","COPY",BODY,{"derivedFrom":makeQuery(id+"F6.opExtrude","SWEPT_BODY",BODY,{"disambiguationData":[OSD([sQuery(id+"F5.wireOp",EDGE,"E0.bottom"),sQuery(id+"F5.wireOp",EDGE,"E0.top"),sQuery(id+"F5.wireOp",EDGE,"E0.left"),sQuery(id+"F5.wireOp",EDGE,"E0.right")])]}),"instanceName":"1"}),"instanceName":"1"});
            var Q9;
            Q9=makeQuery(id+"F35.opPattern","COPY",FACE,{"derivedFrom":makeQuery(id+"F30.opPattern","COPY",FACE,{"derivedFrom":makeQuery(id+"F29.opPattern","COPY",FACE,{"derivedFrom":makeQuery(id+"F24.opExtrude","SWEPT_FACE",FACE,{"disambiguationData":[OSD([sQuery(id+"F23.wireOp",EDGE,"E51"),sQuery(id+"F23.wireOp",EDGE,"E52")])]}),"instanceName":"1"}),"instanceName":"1"}),"instanceName":"1"});
            mirror(context, id + "F38", {"operationType" : NewBodyOperationType.ADD, "entities" : qUnion([Q0, Q1, Q2, Q3, Q4, Q5, Q6, Q7, Q8]), "mirrorPlane" : qUnion([Q9])});
        }
        {
            var Q0;
            Q0=makeQuery(id+"F37.opPattern","COPY",FACE,{"derivedFrom":makeQuery(id+"F30.opPattern","COPY",FACE,{"derivedFrom":makeQuery(id+"F29.opPattern","COPY",FACE,{"derivedFrom":makeQuery(id+"F6.opExtrude","SWEPT_FACE",FACE,{"disambiguationData":[OSD([sQuery(id+"F5.wireOp",EDGE,"E0.right")])]}),"instanceName":"1"}),"instanceName":"1"}),"instanceName":"1"});
            var sketch = newSketch(context, id + "F39", { "sketchPlane" : qUnion([Q0])});
            skText(sketch, "E61", { "text": "W", "fontName": "OpenSans-Bold.ttf"});
            skText(sketch, "E62", { "text": "A", "fontName": "OpenSans-Bold.ttf"});
            skText(sketch, "E63", { "text": "V", "fontName": "OpenSans-Bold.ttf"});
            skText(sketch, "E64", { "text": "E", "fontName": "OpenSans-Bold.ttf"});
            skText(sketch, "E65", { "text": "T", "fontName": "OpenSans-Bold.ttf"});
            skText(sketch, "E66", { "text": "E", "fontName": "OpenSans-Bold.ttf"});
            skText(sketch, "E67", { "text": "C", "fontName": "OpenSans-Bold.ttf"});
            skText(sketch, "E68", { "text": "H", "fontName": "OpenSans-Bold.ttf"});
            skLineSegment(sketch, "E69", {"start": v(-2.9, -5.1) * mm, "end": v(52.21, -5.1) * mm, "construction": true});
            skLineSegment(sketch, "E70", {"start": v(4.55, 14.92) * mm, "end": v(46.32, 14.92) * mm, "construction": true});
            const initialGuessF39  = {"E61": [-0.00476, 0.01492, 1, 0, 0.0065], "E62": [0.01298, 0.01492, 1, 0, 0.0065], "E63": [0.02934, 0.01492, 1, 0, 0.0065], "E64": [0.04632, 0.01492, 1, 0, 0.0065], "E65": [-0.0029, -0.0051, 1, 0, 0.0065], "E66": [0.0137, -0.0051, 1, 0, 0.0065], "E67": [0.02948, -0.0051, 1, 0, 0.0065], "E68": [0.04554, -0.0051, 1, 0, 0.0065]};
            skSetInitialGuess(sketch, initialGuessF39);
            skSolve(sketch);
        }
        {
            var Q0;
            Q0 = qSketchRegion(id + "F39", true);
            extrude(context, id + "F40", {"entities" : qUnion([Q0]), "operationType" : NewBodyOperationType.REMOVE, "oppositeDirection" : true, "depth" : 1 * mm, "offsetDistance" : 25 * mm});
        }
        {
            var Q0;
            Q0=makeQuery(id+"F38.opPattern","COPY",FACE,{"derivedFrom":makeQuery(id+"F6.opExtrude","SWEPT_FACE",FACE,{"disambiguationData":[OSD([sQuery(id+"F5.wireOp",EDGE,"E0.right")])]}),"instanceName":"1"});
            var sketch = newSketch(context, id + "F41", { "sketchPlane" : qUnion([Q0])});
            skText(sketch, "E71", { "text": "3", "fontName": "OpenSans-Bold.ttf"});
            skText(sketch, "E72", { "text": "D", "fontName": "OpenSans-Bold.ttf"});
            const initialGuessF41  = {"E71": [-0.00418, 0.00295, 1, 0, 0.01], "E72": [0.0111, 0.00304, 1, 0, 0.01]};
            skSetInitialGuess(sketch, initialGuessF41);
            skSolve(sketch);
        }
        {
            var Q0;
            Q0 = qSketchRegion(id + "F41", true);
            extrude(context, id + "F42", {"entities" : qUnion([Q0]), "operationType" : NewBodyOperationType.REMOVE, "oppositeDirection" : true, "depth" : 1 * mm, "offsetDistance" : 25 * mm});
        }
        {
            var Q0;
            Q0=makeQuery(id+"F37.opPattern","COPY",FACE,{"derivedFrom":makeQuery(id+"F6.opExtrude","SWEPT_FACE",FACE,{"disambiguationData":[OSD([sQuery(id+"F5.wireOp",EDGE,"E0.right")])]}),"instanceName":"1"});
            var sketch = newSketch(context, id + "F43", { "sketchPlane" : qUnion([Q0])});
            skText(sketch, "E73", { "text": "3", "fontName": "OpenSans-Bold.ttf"});
            skText(sketch, "E74", { "text": "D", "fontName": "OpenSans-Bold.ttf"});
            const initialGuessF43  = {"E73": [-0.0204, 0.00285, 1, 0, 0.01], "E74": [-0.00519, 0.00306, 1, 0, 0.01]};
            skSetInitialGuess(sketch, initialGuessF43);
            skSolve(sketch);
        }
        {
            var Q0;
            Q0 = qSketchRegion(id + "F43", true);
            extrude(context, id + "F44", {"entities" : qUnion([Q0]), "operationType" : NewBodyOperationType.REMOVE, "oppositeDirection" : true, "depth" : 1 * mm, "offsetDistance" : 25 * mm});
        }
    });
